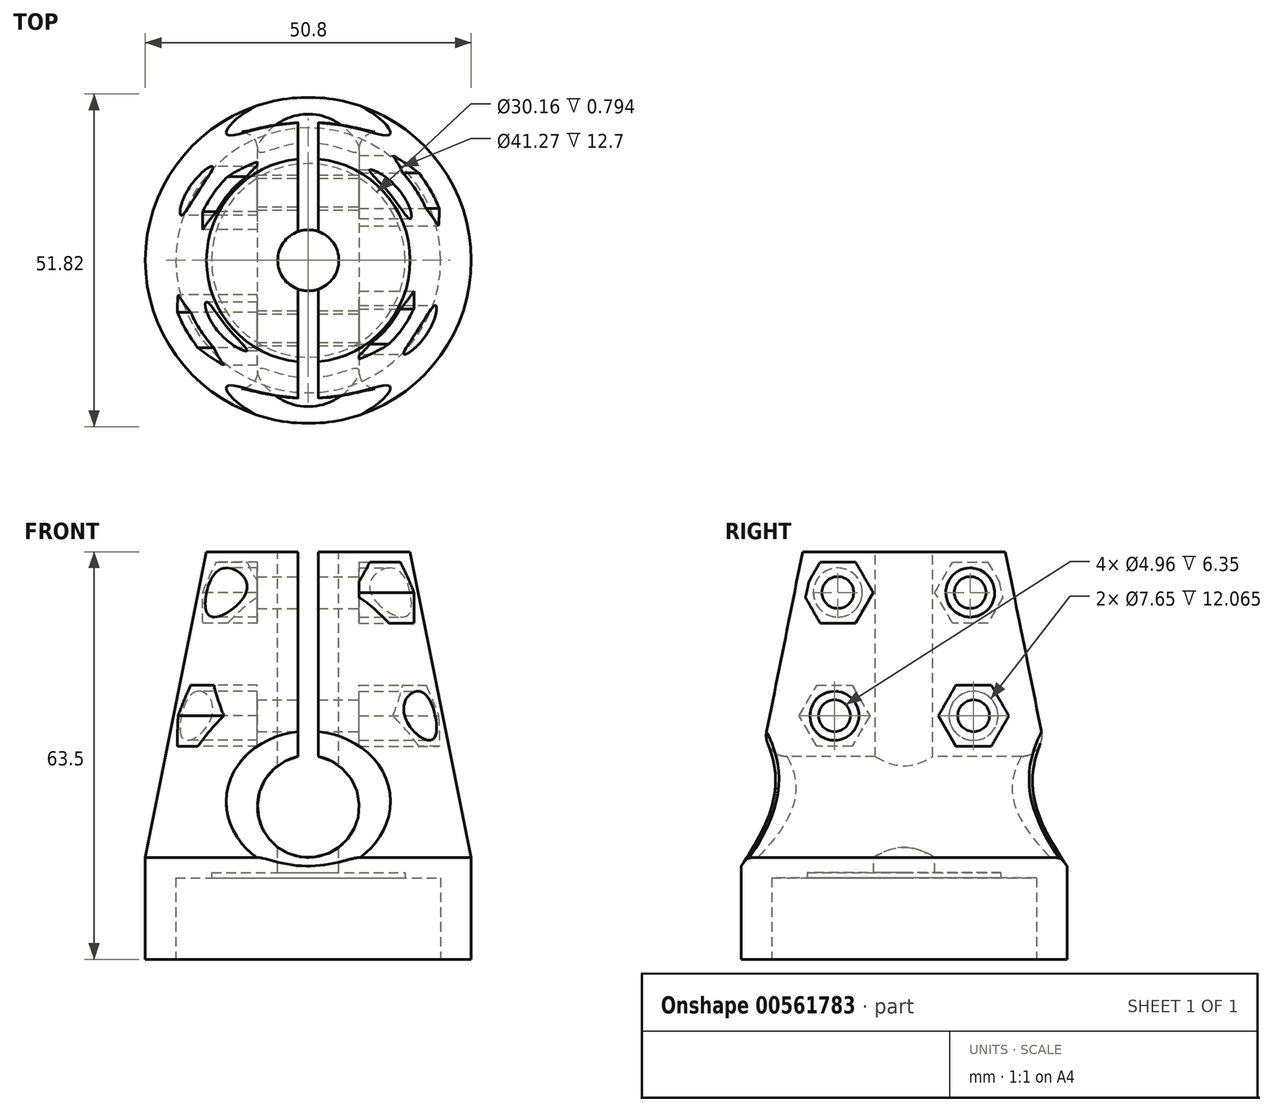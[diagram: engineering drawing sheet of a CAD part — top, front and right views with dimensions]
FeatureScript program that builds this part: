
annotation { "Feature Type Name" : "Feature", "Feature Type Description" : "" }
export const myFeature = defineFeature(function(context is Context, id is Id, definition is map)
    precondition{}
    {
        {
            var Q0;
            Q0=qCreatedBy(makeId("Front.planeOp"),FACE);
            var sketch = newSketch(context, id + "F0", { "sketchPlane" : qUnion([Q0])});
            skLineSegment(sketch, "E0", {"start": v(0, 63.5) * mm, "end": v(15.88, 63.5) * mm});
            skLineSegment(sketch, "E1", {"start": v(15.88, 63.5) * mm, "end": v(25.4, 15.88) * mm});
            skLineSegment(sketch, "E2", {"start": v(25.4, 15.88) * mm, "end": v(25.4, 0) * mm});
            skLineSegment(sketch, "E3", {"start": v(25.4, 0) * mm, "end": v(20.64, 0) * mm});
            skLineSegment(sketch, "E4", {"start": v(20.64, 0) * mm, "end": v(20.64, 12.7) * mm});
            skLineSegment(sketch, "E5", {"start": v(0, 13.5) * mm, "end": v(0, 63.5) * mm});
            skPoint(sketch, "E6.orphan", {"position": v(0, 12.7) * mm});
            skLineSegment(sketch, "E7", {"start": v(9.52, 18.45) * mm, "end": v(9.53, -3.48) * mm, "construction": true});
            skLineSegment(sketch, "E8", {"start": v(20.64, 12.7) * mm, "end": v(9.53, 12.7) * mm, "construction": true});
            skLineSegment(sketch, "E9", {"start": v(20.64, 12.7) * mm, "end": v(15.08, 12.7) * mm});
            skLineSegment(sketch, "E10", {"start": v(0, 13.5) * mm, "end": v(15.08, 13.5) * mm});
            skLineSegment(sketch, "E11", {"start": v(15.08, 13.5) * mm, "end": v(15.08, 12.7) * mm});
            skSolve(sketch);
        }
        {
            var Q0;
            Q0=makeQuery(id+"F0.imprint","IMPRINT",FACE,{"disambiguationData":[TD([[makeQuery(id+"F0.imprint","IMPRINT",EDGE,{"derivedFrom":sQuery(id+"F0.wireOp",EDGE,"E0")}),-1.0]])]});
            var Q1;
            Q1=sQuery(id+"F0.wireOp",EDGE,"E5");
            revolve(context, id + "F1", {"entities" : qUnion([Q0]), "axis" : qUnion([Q1]), "revolveType" : RevolveType.FULL});
        }
        {
            var Q0;
            Q0=makeQuery(id+"F1.opRevolve","SWEPT_FACE",FACE,{"disambiguationData":[OSD([sQuery(id+"F0.wireOp",EDGE,"E0")])]});
            var sketch = newSketch(context, id + "F2", { "sketchPlane" : qUnion([Q0])});
            skCircle(sketch, "E12", {"center": v(0, 0) * mm, "radius": 4.76 * mm});
            skSolve(sketch);
        }
        {
            var Q0;
            Q0=makeQuery(id+"F2.imprint","IMPRINT",FACE,{"disambiguationData":[TD([[makeQuery(id+"F2.imprint","IMPRINT",EDGE,{"derivedFrom":sQuery(id+"F2.wireOp",EDGE,"E12")}),1.0]])]});
            extrude(context, id + "F3", {"entities" : qUnion([Q0]), "operationType" : NewBodyOperationType.REMOVE, "endBound" : BoundingType.THROUGH_ALL, "oppositeDirection" : true, "depth" : 25.4 * mm, "offsetDistance" : 25.4 * mm});
        }
        {
            var Q0;
            Q0=qCreatedBy(makeId("Front.planeOp"),FACE);
            var sketch = newSketch(context, id + "F4", { "sketchPlane" : qUnion([Q0])});
            skCircle(sketch, "E13", {"center": v(0, 23.81) * mm, "radius": 7.94 * mm});
            skSolve(sketch);
        }
        {
            var Q0;
            Q0 = qSketchRegion(id + "F4", true);
            extrude(context, id + "F5", {"entities" : qUnion([Q0]), "operationType" : NewBodyOperationType.REMOVE, "endBound" : BoundingType.SYMMETRIC, "oppositeDirection" : true, "depth" : 50.8 * mm, "offsetDistance" : 25.4 * mm});
        }
        {
            var Q0;
            Q0=makeQuery(id+"F1.opRevolve","SWEPT_FACE",FACE,{"disambiguationData":[OSD([sQuery(id+"F0.wireOp",EDGE,"E0")])]});
            var sketch = newSketch(context, id + "F6", { "sketchPlane" : qUnion([Q0])});
            skLineSegment(sketch, "E14.bottom", {"start": v(0, 0) * mm, "end": v(1.59, 0) * mm});
            skLineSegment(sketch, "E14.top", {"start": v(0, 25.4) * mm, "end": v(1.59, 25.4) * mm});
            skLineSegment(sketch, "E14.left", {"start": v(0, 0) * mm, "end": v(0, 25.4) * mm});
            skLineSegment(sketch, "E14.right", {"start": v(1.59, 0) * mm, "end": v(1.59, 25.4) * mm});
            skLineSegment(sketch, "E15.MirrorCS", {"start": v(0, -25.4) * mm, "end": v(1.59, -25.4) * mm});
            skLineSegment(sketch, "E16.MirrorCS", {"start": v(1.59, 0) * mm, "end": v(1.59, -25.4) * mm});
            skLineSegment(sketch, "E17.MirrorCS", {"start": v(0, 0) * mm, "end": v(0, -25.4) * mm});
            skLineSegment(sketch, "E18.MirrorCS", {"start": v(0, 25.4) * mm, "end": v(-1.59, 25.4) * mm});
            skLineSegment(sketch, "E19.MirrorCS", {"start": v(-1.59, 0) * mm, "end": v(-1.59, 25.4) * mm});
            skLineSegment(sketch, "E20.MirrorCS", {"start": v(-1.59, 0) * mm, "end": v(-1.59, -25.4) * mm});
            skLineSegment(sketch, "E21.MirrorCS", {"start": v(0, -25.4) * mm, "end": v(-1.59, -25.4) * mm});
            skSolve(sketch);
        }
        {
            var Q0;
            Q0 = qSketchRegion(id + "F6", true);
            extrude(context, id + "F7", {"entities" : qUnion([Q0]), "operationType" : NewBodyOperationType.REMOVE, "oppositeDirection" : true, "depth" : 38.1 * mm, "offsetDistance" : 25.4 * mm});
        }
        {
            var Q0;
            Q0=makeQuery(id+"F7.boolean.opBoolean","SPLIT",FACE,{"disambiguationData":[TD([makeQuery(id+"F7.opExtrude","SWEPT_FACE",FACE,{"disambiguationData":[OSD([sQuery(id+"F6.wireOp",EDGE,"E19.MirrorCS"),sQuery(id+"F6.wireOp",EDGE,"E20.MirrorCS")])]})])],"derivedFrom":makeQuery(id+"F1.opRevolve","SWEPT_FACE",FACE,{"disambiguationData":[OSD([sQuery(id+"F0.wireOp",EDGE,"E0")])]})});
            cPlane(context, id + "F8", {"entities" : qUnion([Q0]), "cplaneType" : CPlaneType.OFFSET, "offset" : 19.05 * mm, "width" : 152.4 * mm, "height" : 152.4 * mm});
        }
        {
            var Q0;
            Q0=qCreatedBy(id+"F8.planeOp",FACE);
            var sketch = newSketch(context, id + "F9", { "sketchPlane" : qUnion([Q0])});
            skCircle(sketch, "E22", {"center": v(0, 0) * mm, "radius": 4.76 * mm});
            skSolve(sketch);
        }
        {
            var Q0;
            Q0=makeQuery(id+"F7.boolean.opBoolean","COPY",FACE,{"disambiguationData":[OD(0.0)],"derivedFrom":makeQuery(id+"F7.opExtrude","SWEPT_FACE",FACE,{"disambiguationData":[OSD([sQuery(id+"F6.wireOp",EDGE,"E19.MirrorCS"),sQuery(id+"F6.wireOp",EDGE,"E20.MirrorCS")])]})});
            var sketch = newSketch(context, id + "F10", { "sketchPlane" : qUnion([Q0])});
            skCircle(sketch, "E23", {"center": v(-10.84, 37.94) * mm, "radius": 2.48 * mm});
            skLineSegment(sketch, "E24", {"start": v(-10.14, 63.5) * mm, "end": v(-10.84, 37.94) * mm, "construction": true});
            skCircle(sketch, "E25", {"center": v(-10.32, 57.15) * mm, "radius": 2.48 * mm});
            skCircle(sketch, "E26.MirrorC", {"center": v(10.32, 57.15) * mm, "radius": 2.48 * mm});
            skCircle(sketch, "E27.MirrorC", {"center": v(10.84, 37.94) * mm, "radius": 2.48 * mm});
            skSolve(sketch);
        }
        {
            var Q0;
            Q0 = qSketchRegion(id + "F10", true);
            extrude(context, id + "F11", {"entities" : qUnion([Q0]), "operationType" : NewBodyOperationType.REMOVE, "endBound" : BoundingType.SYMMETRIC, "oppositeDirection" : true, "depth" : 76.2 * mm, "offsetDistance" : 25.4 * mm});
        }
        {
            var Q0;
            Q0=qCreatedBy(makeId("Right.planeOp"),FACE);
            cPlane(context, id + "F12", {"entities" : qUnion([Q0]), "cplaneType" : CPlaneType.OFFSET, "offset" : 50.8 * mm, "width" : 152.4 * mm, "height" : 152.4 * mm});
        }
        {
            var Q0;
            Q0=qCreatedBy(id+"F12.planeOp",FACE);
            var sketch = newSketch(context, id + "F13", { "sketchPlane" : qUnion([Q0])});
            skCircle(sketch, "E28", {"center": v(-10.84, 37.94) * mm, "radius": 3.83 * mm});
            skCircle(sketch, "E29", {"center": v(10.32, 57.15) * mm, "radius": 3.83 * mm});
            skCircle(sketch, "E30.cCircle", {"center": v(-10.32, 57.15) * mm, "radius": 4.76 * mm, "construction": true});
            skLineSegment(sketch, "E30.0", {"start": v(-13.07, 52.39) * mm, "end": v(-15.82, 57.15) * mm});
            skLineSegment(sketch, "E30.1", {"start": v(-15.82, 57.15) * mm, "end": v(-13.07, 61.91) * mm});
            skLineSegment(sketch, "E30.2", {"start": v(-13.07, 61.91) * mm, "end": v(-7.57, 61.91) * mm});
            skLineSegment(sketch, "E30.3", {"start": v(-7.57, 61.91) * mm, "end": v(-4.82, 57.15) * mm});
            skLineSegment(sketch, "E30.4", {"start": v(-4.82, 57.15) * mm, "end": v(-7.57, 52.39) * mm});
            skLineSegment(sketch, "E30.5", {"start": v(-7.57, 52.39) * mm, "end": v(-13.07, 52.39) * mm});
            skPoint(sketch, "E30.0.midPoint", {"position": v(-14.44, 54.77) * mm});
            skCircle(sketch, "E31.cCircle", {"center": v(10.84, 37.94) * mm, "radius": 4.76 * mm, "construction": true});
            skLineSegment(sketch, "E31.0", {"start": v(16.34, 37.94) * mm, "end": v(13.59, 33.18) * mm});
            skLineSegment(sketch, "E31.1", {"start": v(13.59, 33.18) * mm, "end": v(8.1, 33.18) * mm});
            skLineSegment(sketch, "E31.2", {"start": v(8.1, 33.18) * mm, "end": v(5.34, 37.94) * mm});
            skLineSegment(sketch, "E31.3", {"start": v(5.34, 37.94) * mm, "end": v(8.1, 42.7) * mm});
            skLineSegment(sketch, "E31.4", {"start": v(8.1, 42.7) * mm, "end": v(13.59, 42.7) * mm});
            skLineSegment(sketch, "E31.5", {"start": v(13.59, 42.7) * mm, "end": v(16.34, 37.94) * mm});
            skPoint(sketch, "E31.0.midPoint", {"position": v(14.96, 35.56) * mm});
            skSolve(sketch);
        }
        {
            var Q0;
            Q0=makeQuery(id+"F13.imprint","IMPRINT",FACE,{"disambiguationData":[TD([[makeQuery(id+"F13.imprint","IMPRINT",EDGE,{"derivedFrom":sQuery(id+"F13.wireOp",EDGE,"E28")}),1.0]])]});
            var Q1;
            Q1=makeQuery(id+"F13.imprint","IMPRINT",FACE,{"disambiguationData":[TD([[makeQuery(id+"F13.imprint","IMPRINT",EDGE,{"derivedFrom":sQuery(id+"F13.wireOp",EDGE,"E31.0")}),-1.0]])]});
            var Q2;
            Q2=makeQuery(id+"F13.imprint","IMPRINT",FACE,{"disambiguationData":[TD([[makeQuery(id+"F13.imprint","IMPRINT",EDGE,{"derivedFrom":sQuery(id+"F13.wireOp",EDGE,"E30.0")}),-1.0]])]});
            var Q3;
            Q3=makeQuery(id+"F13.imprint","IMPRINT",FACE,{"disambiguationData":[TD([[makeQuery(id+"F13.imprint","IMPRINT",EDGE,{"derivedFrom":sQuery(id+"F13.wireOp",EDGE,"E29")}),1.0]])]});
            var Q4;
            Q4=makeQuery(id+"F7.boolean.opBoolean","COPY",FACE,{"disambiguationData":[OD(0.0)],"derivedFrom":makeQuery(id+"F7.opExtrude","SWEPT_FACE",FACE,{"disambiguationData":[OSD([sQuery(id+"F6.wireOp",EDGE,"E14.right"),sQuery(id+"F6.wireOp",EDGE,"E16.MirrorCS")])]})});
            extrude(context, id + "F14", {"entities" : qUnion([Q0, Q1, Q2, Q3]), "endBound" : BoundingType.UP_TO_SURFACE, "oppositeDirection" : true, "depth" : 25.4 * mm, "endBoundEntityFace" : qUnion([Q4]), "hasOffset" : true, "offsetDistance" : 6.35 * mm});
        }
        {
            var Q0;
            Q0=makeQuery(id+"F14.opExtrude","SWEPT_BODY",BODY,{"disambiguationData":[OSD([sQuery(id+"F13.wireOp",EDGE,"E30.0"),sQuery(id+"F13.wireOp",EDGE,"E30.1"),sQuery(id+"F13.wireOp",EDGE,"E30.2"),sQuery(id+"F13.wireOp",EDGE,"E30.3"),sQuery(id+"F13.wireOp",EDGE,"E30.4"),sQuery(id+"F13.wireOp",EDGE,"E30.5")])]});
            var Q1;
            Q1=makeQuery(id+"F14.opExtrude","SWEPT_BODY",BODY,{"disambiguationData":[OSD([sQuery(id+"F13.wireOp",EDGE,"E29")])]});
            var Q2;
            Q2=makeQuery(id+"F14.opExtrude","SWEPT_BODY",BODY,{"disambiguationData":[OSD([sQuery(id+"F13.wireOp",EDGE,"E28")])]});
            var Q3;
            Q3=makeQuery(id+"F14.opExtrude","SWEPT_BODY",BODY,{"disambiguationData":[OSD([sQuery(id+"F13.wireOp",EDGE,"E31.0"),sQuery(id+"F13.wireOp",EDGE,"E31.1"),sQuery(id+"F13.wireOp",EDGE,"E31.2"),sQuery(id+"F13.wireOp",EDGE,"E31.3"),sQuery(id+"F13.wireOp",EDGE,"E31.4"),sQuery(id+"F13.wireOp",EDGE,"E31.5")])]});
            var Q4;
            Q4=sQuery(id+"F0.wireOp",EDGE,"E5");
            circularPattern(context, id + "F15", {"entities" : qUnion([Q0, Q1, Q2, Q3]), "axis" : qUnion([Q4]), "angle" : 360 * degree, "instanceCount" : 2, "equalSpace" : true});
        }
        {
            var Q0;
            Q0=makeQuery(id+"F14.opExtrude","SWEPT_BODY",BODY,{"disambiguationData":[OSD([sQuery(id+"F13.wireOp",EDGE,"E31.0"),sQuery(id+"F13.wireOp",EDGE,"E31.1"),sQuery(id+"F13.wireOp",EDGE,"E31.2"),sQuery(id+"F13.wireOp",EDGE,"E31.3"),sQuery(id+"F13.wireOp",EDGE,"E31.4"),sQuery(id+"F13.wireOp",EDGE,"E31.5")])]});
            var Q1;
            Q1=makeQuery(id+"F14.opExtrude","SWEPT_BODY",BODY,{"disambiguationData":[OSD([sQuery(id+"F13.wireOp",EDGE,"E30.0"),sQuery(id+"F13.wireOp",EDGE,"E30.1"),sQuery(id+"F13.wireOp",EDGE,"E30.2"),sQuery(id+"F13.wireOp",EDGE,"E30.3"),sQuery(id+"F13.wireOp",EDGE,"E30.4"),sQuery(id+"F13.wireOp",EDGE,"E30.5")])]});
            var Q2;
            Q2=makeQuery(id+"F14.opExtrude","SWEPT_BODY",BODY,{"disambiguationData":[OSD([sQuery(id+"F13.wireOp",EDGE,"E29")])]});
            var Q3;
            Q3=makeQuery(id+"F14.opExtrude","SWEPT_BODY",BODY,{"disambiguationData":[OSD([sQuery(id+"F13.wireOp",EDGE,"E28")])]});
            var Q4;
            Q4=makeQuery(id+"F15.opPattern","COPY",BODY,{"derivedFrom":makeQuery(id+"F14.opExtrude","SWEPT_BODY",BODY,{"disambiguationData":[OSD([sQuery(id+"F13.wireOp",EDGE,"E28")])]}),"instanceName":"1"});
            var Q5;
            Q5=makeQuery(id+"F15.opPattern","COPY",BODY,{"derivedFrom":makeQuery(id+"F14.opExtrude","SWEPT_BODY",BODY,{"disambiguationData":[OSD([sQuery(id+"F13.wireOp",EDGE,"E30.0"),sQuery(id+"F13.wireOp",EDGE,"E30.1"),sQuery(id+"F13.wireOp",EDGE,"E30.2"),sQuery(id+"F13.wireOp",EDGE,"E30.3"),sQuery(id+"F13.wireOp",EDGE,"E30.4"),sQuery(id+"F13.wireOp",EDGE,"E30.5")])]}),"instanceName":"1"});
            var Q6;
            Q6=makeQuery(id+"F15.opPattern","COPY",BODY,{"derivedFrom":makeQuery(id+"F14.opExtrude","SWEPT_BODY",BODY,{"disambiguationData":[OSD([sQuery(id+"F13.wireOp",EDGE,"E31.0"),sQuery(id+"F13.wireOp",EDGE,"E31.1"),sQuery(id+"F13.wireOp",EDGE,"E31.2"),sQuery(id+"F13.wireOp",EDGE,"E31.3"),sQuery(id+"F13.wireOp",EDGE,"E31.4"),sQuery(id+"F13.wireOp",EDGE,"E31.5")])]}),"instanceName":"1"});
            var Q7;
            Q7=makeQuery(id+"F15.opPattern","COPY",BODY,{"derivedFrom":makeQuery(id+"F14.opExtrude","SWEPT_BODY",BODY,{"disambiguationData":[OSD([sQuery(id+"F13.wireOp",EDGE,"E29")])]}),"instanceName":"1"});
            var Q8;
            Q8=makeQuery(id+"F1.opRevolve","SWEPT_BODY",BODY,{"disambiguationData":[OSD([sQuery(id+"F0.wireOp",EDGE,"E0"),sQuery(id+"F0.wireOp",EDGE,"E1"),sQuery(id+"F0.wireOp",EDGE,"E2"),sQuery(id+"F0.wireOp",EDGE,"E3"),sQuery(id+"F0.wireOp",EDGE,"E4"),sQuery(id+"F0.wireOp",EDGE,"E5"),sQuery(id+"F0.wireOp",EDGE,"E9"),sQuery(id+"F0.wireOp",EDGE,"E10"),sQuery(id+"F0.wireOp",EDGE,"E11")])]});
            booleanBodies(context, id + "F16", {"operationType" : BooleanOperationType.SUBTRACTION, "tools" : qUnion([Q0, Q1, Q2, Q3, Q4, Q5, Q6, Q7]), "targets" : qUnion([Q8])});
        }
        {
            var Q0;
            {var subQ0=makeQuery(id+"F1.opRevolve","SWEPT_FACE",FACE,{"disambiguationData":[OSD([sQuery(id+"F0.wireOp",EDGE,"E1")])]});var subQ1=makeQuery(id+"F5.opExtrude","SWEPT_FACE",FACE,{"disambiguationData":[OSD([sQuery(id+"F4.wireOp",EDGE,"E13")])]});Q0=makeQuery(id+"F7.boolean.opBoolean","SPLIT",EDGE,{"disambiguationData":[TD([makeQuery(id+"F7.opExtrude","SWEPT_FACE",FACE,{"disambiguationData":[OSD([sQuery(id+"F6.wireOp",EDGE,"E14.right"),sQuery(id+"F6.wireOp",EDGE,"E16.MirrorCS")])]})])],"derivedFrom":makeQuery(id+"F5.boolean.opBoolean","INTERSECT",EDGE,{"disambiguationData":[OD(1.0)],"derivedFrom":[subQ0,subQ1]})});}
            var Q1;
            {var subQ0=makeQuery(id+"F1.opRevolve","SWEPT_FACE",FACE,{"disambiguationData":[OSD([sQuery(id+"F0.wireOp",EDGE,"E1")])]});var subQ1=makeQuery(id+"F5.opExtrude","SWEPT_FACE",FACE,{"disambiguationData":[OSD([sQuery(id+"F4.wireOp",EDGE,"E13")])]});Q1=makeQuery(id+"F7.boolean.opBoolean","SPLIT",EDGE,{"disambiguationData":[TD([makeQuery(id+"F7.opExtrude","SWEPT_FACE",FACE,{"disambiguationData":[OSD([sQuery(id+"F6.wireOp",EDGE,"E19.MirrorCS"),sQuery(id+"F6.wireOp",EDGE,"E20.MirrorCS")])]})])],"derivedFrom":makeQuery(id+"F5.boolean.opBoolean","INTERSECT",EDGE,{"disambiguationData":[OD(0.0)],"derivedFrom":[subQ0,subQ1]})});}
            fillet(context, id + "F17", {"entities" : qUnion([Q0, Q1]), "radius" : 3.17 * mm, "tangentPropagation" : true, "allowEdgeOverflow" : false});
        }
    });
